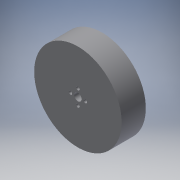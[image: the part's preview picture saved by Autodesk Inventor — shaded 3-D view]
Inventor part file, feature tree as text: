
AUTODESK INVENTOR PART (.ipt)
format: ipt  version: 2016 (Build 200138000, 138)  size: 99,328 bytes
history: native  units: mm
features: reference x5, extrude x1, sketch x1
ambient origin geometry x8: Origin, YZ Plane, XZ Plane, XY Plane, X Axis, Y Axis, Z Axis, Center Point
bodies: Body1 (feature_tree)
feature tree (7):
  extrude  "Extrusion2"  Depth=26.0mm TaperAngle=0.0deg
  sketch  "Sketch1"  dims[d0=94.0mm d3=26.0mm d4=0.0mm]
  reference  "Reference1"
  reference  "Reference2"
  reference  "Reference3"
  reference  "Reference4"
  reference  "Reference5"
